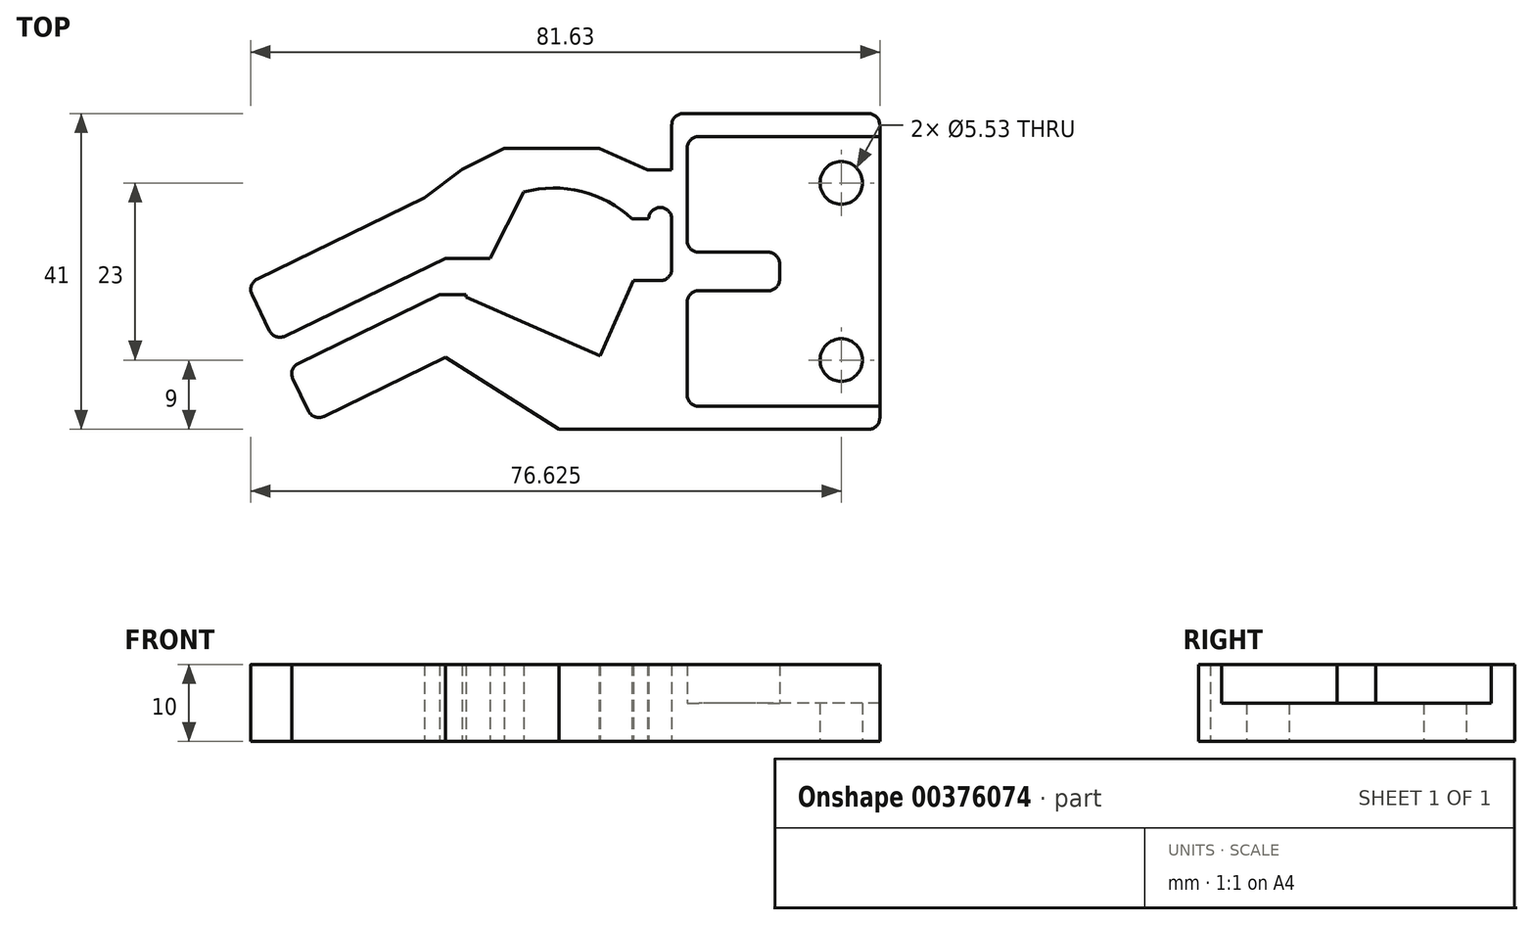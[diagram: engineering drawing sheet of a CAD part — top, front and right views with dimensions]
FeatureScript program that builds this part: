
annotation { "Feature Type Name" : "Feature", "Feature Type Description" : "" }
export const myFeature = defineFeature(function(context is Context, id is Id, definition is map)
    precondition{}
    {
        {
            var Q0;
            Q0=qCreatedBy(makeId("Top.planeOp"),FACE);
            var sketch = newSketch(context, id + "F0", { "sketchPlane" : qUnion([Q0])});
            skLineSegment(sketch, "E0", {"start": v(-32.48, 19.3) * mm, "end": v(-28.98, 19.3) * mm});
            skLineSegment(sketch, "E1", {"start": v(-27.48, 20.8) * mm, "end": v(-27.48, 27.3) * mm});
            skLineSegment(sketch, "E2", {"start": v(-25.48, 36.5) * mm, "end": v(-25.48, 24.5) * mm});
            skLineSegment(sketch, "E3", {"start": v(-42.11, 0) * mm, "end": v(-56.83, 9.37) * mm});
            skLineSegment(sketch, "E4", {"start": v(-36.7, 9.69) * mm, "end": v(-32.48, 19.3) * mm});
            skLineSegment(sketch, "E5", {"start": v(-25.48, 41) * mm, "end": v(-1.98, 41) * mm});
            skLineSegment(sketch, "E6", {"start": v(-0.48, 39.5) * mm, "end": v(-0.48, 38) * mm});
            skLineSegment(sketch, "E7", {"start": v(-0.48, 38) * mm, "end": v(-23.98, 38) * mm});
            skLineSegment(sketch, "E8", {"start": v(-23.98, 3) * mm, "end": v(-0.48, 3) * mm});
            skLineSegment(sketch, "E9", {"start": v(-0.48, 3) * mm, "end": v(-0.48, 1.5) * mm});
            skLineSegment(sketch, "E10", {"start": v(-1.98, 0) * mm, "end": v(-18.5, 0) * mm});
            skPoint(sketch, "E11", {"position": v(-46.67, 30.8) * mm});
            skLineSegment(sketch, "E12", {"start": v(-46.29, 20.94) * mm, "end": v(-46.29, 20.94) * mm});
            skLineSegment(sketch, "E13", {"start": v(-0.48, 38) * mm, "end": v(-0.48, 37.95) * mm});
            skPoint(sketch, "E14", {"position": v(-5.48, 32) * mm});
            skPoint(sketch, "E15", {"position": v(-5.48, 9) * mm});
            skCircle(sketch, "E16", {"center": v(-5.48, 32) * mm, "radius": 2.76 * mm});
            skLineSegment(sketch, "E17", {"start": v(-0.48, 3.05) * mm, "end": v(-0.48, 3) * mm});
            skLineSegment(sketch, "E18", {"start": v(-27.48, 33.71) * mm, "end": v(-30.64, 33.71) * mm});
            skLineSegment(sketch, "E19", {"start": v(-30.64, 33.71) * mm, "end": v(-36.93, 36.47) * mm});
            skLineSegment(sketch, "E20", {"start": v(-36.93, 36.47) * mm, "end": v(-49.2, 36.47) * mm});
            skLineSegment(sketch, "E21.trimOffspring", {"start": v(-28.5, 0) * mm, "end": v(-42.11, 0) * mm});
            skLineSegment(sketch, "E22", {"start": v(-28.5, 0) * mm, "end": v(-18.5, 0) * mm});
            skLineSegment(sketch, "E23.trimOffspring", {"start": v(-27.48, 33.71) * mm, "end": v(-27.48, 39.3) * mm});
            skLineSegment(sketch, "E24", {"start": v(-0.48, 38) * mm, "end": v(-0.48, 3.05) * mm});
            skCircle(sketch, "E25", {"center": v(-5.48, 9) * mm, "radius": 2.76 * mm});
            skLineSegment(sketch, "E26", {"start": v(-23.98, 23) * mm, "end": v(-14.98, 23) * mm});
            skLineSegment(sketch, "E27", {"start": v(-13.48, 21.5) * mm, "end": v(-13.48, 19.5) * mm});
            skLineSegment(sketch, "E28", {"start": v(-14.98, 18) * mm, "end": v(-23.98, 18) * mm});
            skArc(sketch, "E29", {"start": v(-32.63, 27.3) * mm, "mid": v(-39.19, 30.9) * mm, "end": v(-46.67, 30.8) * mm});
            skLineSegment(sketch, "E30", {"start": v(-36.7, 9.69) * mm, "end": v(-36.76, 9.54) * mm});
            skLineSegment(sketch, "E31", {"start": v(-36.76, 9.54) * mm, "end": v(-54.17, 17.16) * mm});
            skLineSegment(sketch, "E32.trimOffspring", {"start": v(-25.48, 16.5) * mm, "end": v(-25.48, 4.5) * mm});
            skPoint(sketch, "E33.visualSharp", {"position": v(-25.48, 23) * mm});
            skArc(sketch, "E33.filletArc", {"start": v(-25.48, 24.5) * mm, "mid": v(-25.05, 23.44) * mm, "end": v(-23.98, 23) * mm});
            skPoint(sketch, "E34.visualSharp", {"position": v(-25.48, 18) * mm});
            skArc(sketch, "E34.filletArc", {"start": v(-23.98, 18) * mm, "mid": v(-25.05, 17.56) * mm, "end": v(-25.48, 16.5) * mm});
            skPoint(sketch, "E35.visualSharp", {"position": v(-13.48, 23) * mm});
            skArc(sketch, "E35.filletArc", {"start": v(-13.48, 21.5) * mm, "mid": v(-13.92, 22.56) * mm, "end": v(-14.98, 23) * mm});
            skPoint(sketch, "E36.visualSharp", {"position": v(-13.48, 18) * mm});
            skArc(sketch, "E36.filletArc", {"start": v(-14.98, 18) * mm, "mid": v(-13.92, 18.44) * mm, "end": v(-13.48, 19.5) * mm});
            skPoint(sketch, "E37.visualSharp", {"position": v(-25.48, 38) * mm});
            skArc(sketch, "E37.filletArc", {"start": v(-23.98, 38) * mm, "mid": v(-25.05, 37.56) * mm, "end": v(-25.48, 36.5) * mm});
            skPoint(sketch, "E38.visualSharp", {"position": v(-25.48, 3) * mm});
            skArc(sketch, "E38.filletArc", {"start": v(-25.48, 4.5) * mm, "mid": v(-25.05, 3.44) * mm, "end": v(-23.98, 3) * mm});
            skLineSegment(sketch, "E39", {"start": v(-25.48, 41) * mm, "end": v(-25.98, 41) * mm});
            skLineSegment(sketch, "E40", {"start": v(-27.48, 39.5) * mm, "end": v(-27.48, 39.3) * mm});
            skPoint(sketch, "E41.visualSharp", {"position": v(-27.48, 41) * mm});
            skArc(sketch, "E41.filletArc", {"start": v(-25.98, 41) * mm, "mid": v(-27.05, 40.56) * mm, "end": v(-27.48, 39.5) * mm});
            skLineSegment(sketch, "E42", {"start": v(-81.96, 17.5) * mm, "end": v(-80.43, 14.35) * mm});
            skLineSegment(sketch, "E43.trimOffspring", {"start": v(-76.65, 6.56) * mm, "end": v(-75.27, 3.71) * mm});
            skLineSegment(sketch, "E44", {"start": v(-46.67, 30.8) * mm, "end": v(-50.2, 23.94) * mm});
            skPoint(sketch, "E45.visualSharp", {"position": v(-0.48, 41) * mm});
            skArc(sketch, "E45.filletArc", {"start": v(-0.48, 39.5) * mm, "mid": v(-0.92, 40.56) * mm, "end": v(-1.98, 41) * mm});
            skPoint(sketch, "E46.visualSharp", {"position": v(-0.48, 0) * mm});
            skArc(sketch, "E46.filletArc", {"start": v(-1.98, 0) * mm, "mid": v(-0.92, 0.44) * mm, "end": v(-0.48, 1.5) * mm});
            skPoint(sketch, "E47.visualSharp", {"position": v(-27.48, 19.3) * mm});
            skArc(sketch, "E47.filletArc", {"start": v(-28.98, 19.3) * mm, "mid": v(-27.92, 19.75) * mm, "end": v(-27.48, 20.8) * mm});
            skLineSegment(sketch, "E48", {"start": v(-32.63, 27.3) * mm, "end": v(-30.48, 27.3) * mm});
            skPoint(sketch, "E49", {"position": v(-28.98, 27.3) * mm});
            skArc(sketch, "E50", {"start": v(-27.48, 27.3) * mm, "mid": v(-28.98, 28.8) * mm, "end": v(-30.48, 27.3) * mm});
            skLineSegment(sketch, "E51", {"start": v(-72.62, 1.7) * mm, "end": v(-56.83, 9.37) * mm});
            skLineSegment(sketch, "E52", {"start": v(-75.27, 3.71) * mm, "end": v(-74.63, 2.4) * mm});
            skArc(sketch, "E53.filletArc", {"start": v(-74.63, 2.4) * mm, "mid": v(-73.77, 1.63) * mm, "end": v(-72.62, 1.7) * mm});
            skLineSegment(sketch, "E54", {"start": v(-57.6, 17.47) * mm, "end": v(-75.95, 8.56) * mm});
            skArc(sketch, "E55.filletArc", {"start": v(-75.95, 8.56) * mm, "mid": v(-76.71, 7.7) * mm, "end": v(-76.65, 6.56) * mm});
            skLineSegment(sketch, "E56", {"start": v(-57.6, 17.47) * mm, "end": v(-54.17, 17.47) * mm});
            skPoint(sketch, "E57", {"position": v(-54.17, 17.47) * mm});
            skLineSegment(sketch, "E58", {"start": v(-54.17, 17.47) * mm, "end": v(-54.17, 17.16) * mm});
            skLineSegment(sketch, "E59", {"start": v(-80.43, 14.35) * mm, "end": v(-79.68, 12.82) * mm});
            skLineSegment(sketch, "E60", {"start": v(-77.68, 12.12) * mm, "end": v(-56.88, 22.22) * mm});
            skArc(sketch, "E61.filletArc", {"start": v(-79.68, 12.82) * mm, "mid": v(-78.82, 12.05) * mm, "end": v(-77.68, 12.12) * mm});
            skLineSegment(sketch, "E62", {"start": v(-50.2, 23.94) * mm, "end": v(-51.08, 22.22) * mm});
            skLineSegment(sketch, "E63", {"start": v(-51.08, 22.22) * mm, "end": v(-56.88, 22.22) * mm});
            skLineSegment(sketch, "E64", {"start": v(-81.26, 19.5) * mm, "end": v(-59.57, 30.03) * mm});
            skLineSegment(sketch, "E65", {"start": v(-49.2, 36.47) * mm, "end": v(-54.72, 33.77) * mm});
            skLineSegment(sketch, "E66", {"start": v(-54.72, 33.77) * mm, "end": v(-59.57, 30.03) * mm});
            skArc(sketch, "E67.filletArc", {"start": v(-81.26, 19.5) * mm, "mid": v(-82.02, 18.64) * mm, "end": v(-81.96, 17.5) * mm});
            skSolve(sketch);
        }
        {
            var Q0;
            Q0=makeQuery(id+"F0.imprint","IMPRINT",FACE,{"disambiguationData":[TD([[makeQuery(id+"F0.imprint","IMPRINT",EDGE,{"derivedFrom":sQuery(id+"F0.wireOp",EDGE,"FPX6U4WJ-Njni-V2VI-gTjT-Pai6s9Fpejf8")}),-1.0]])]});
            var Q1;
            Q1=makeQuery(id+"F0.imprint","IMPRINT",FACE,{"disambiguationData":[TD([[makeQuery(id+"F0.imprint","IMPRINT",EDGE,{"derivedFrom":sQuery(id+"F0.wireOp",EDGE,"E0")}),-1.0]])]});
            extrude(context, id + "F1", {"entities" : qUnion([Q0, Q1]), "depth" : 10 * mm});
        }
        {
            var Q0;
            Q0=makeQuery(id+"F0.imprint","IMPRINT",FACE,{"disambiguationData":[TD([[makeQuery(id+"F0.imprint","IMPRINT",EDGE,{"derivedFrom":sQuery(id+"F0.wireOp",EDGE,"E2")}),1.0]])]});
            extrude(context, id + "F2", {"entities" : qUnion([Q0]), "operationType" : NewBodyOperationType.ADD, "depth" : 5 * mm});
        }
    });
